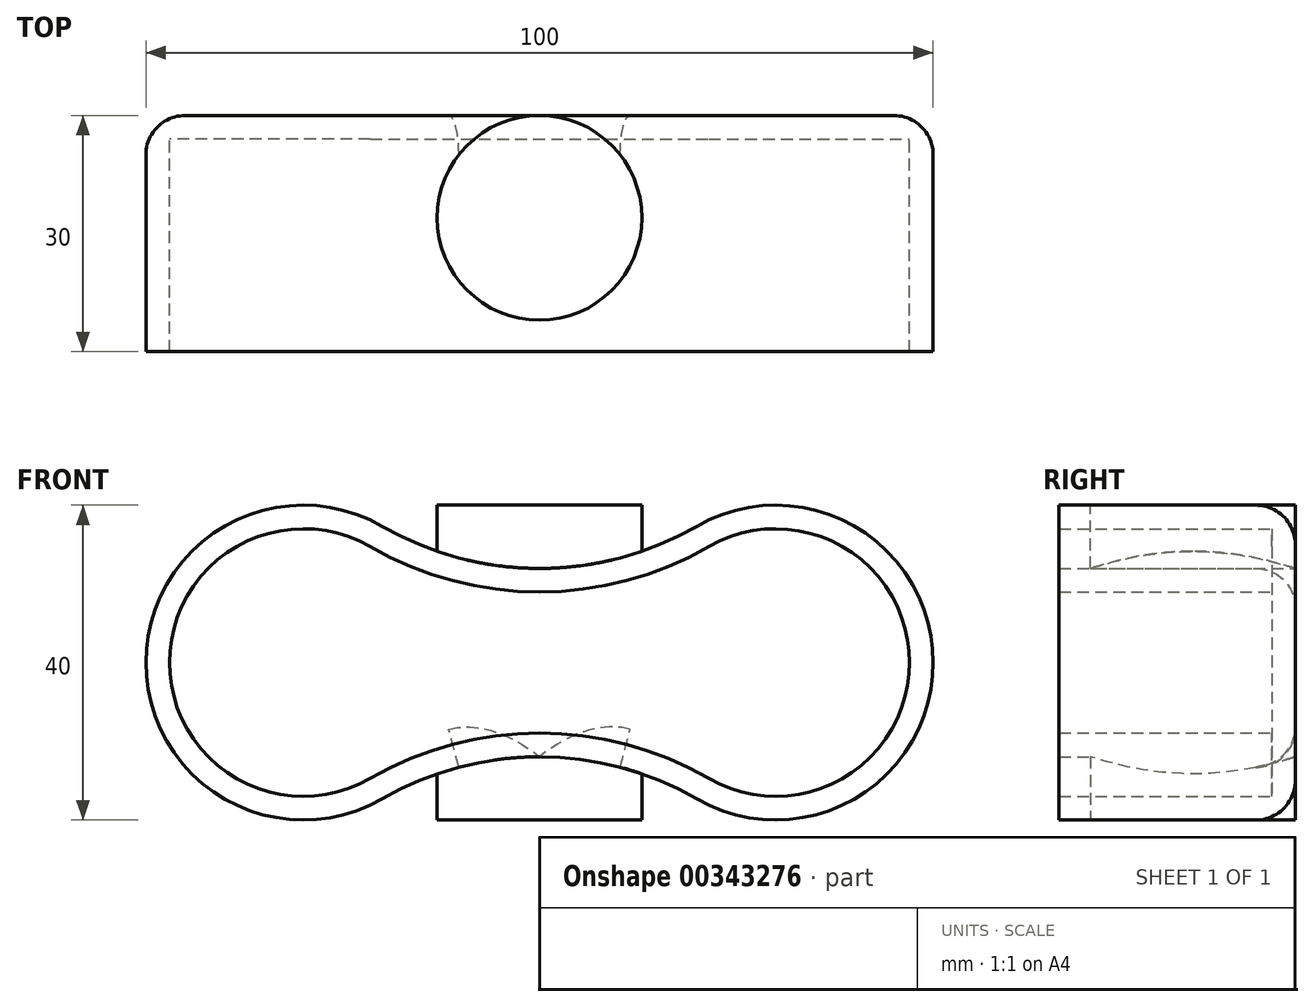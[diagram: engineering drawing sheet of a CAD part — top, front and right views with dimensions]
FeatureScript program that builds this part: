
annotation { "Feature Type Name" : "Feature", "Feature Type Description" : "" }
export const myFeature = defineFeature(function(context is Context, id is Id, definition is map)
    precondition{}
    {
        {
            var Q0;
            Q0=qCreatedBy(makeId("Front.planeOp"),FACE);
            var sketch = newSketch(context, id + "F0", { "sketchPlane" : qUnion([Q0])});
            skArc(sketch, "E0", {"start": v(-20, 17.32) * mm, "mid": v(-50, 0) * mm, "end": v(-20, -17.32) * mm});
            skLineSegment(sketch, "E1", {"start": v(0, 56.7) * mm, "end": v(0, -51.8) * mm, "construction": true});
            skLineSegment(sketch, "E2", {"start": v(-30, 42.91) * mm, "end": v(-30, -37.47) * mm, "construction": true});
            skLineSegment(sketch, "E3", {"start": v(-82.46, 0) * mm, "end": v(56.18, 0) * mm, "construction": true});
            skArc(sketch, "E4", {"start": v(20, -17.32) * mm, "mid": v(0, -11.96) * mm, "end": v(-20, -17.32) * mm});
            skArc(sketch, "E5", {"start": v(20, -17.32) * mm, "mid": v(50, 0) * mm, "end": v(20, 17.32) * mm});
            skArc(sketch, "E6", {"start": v(-20, 17.32) * mm, "mid": v(0, 11.96) * mm, "end": v(20, 17.32) * mm});
            skLineSegment(sketch, "E7", {"start": v(-11.98, 0) * mm, "end": v(72.4, 0) * mm, "construction": true});
            skLineSegment(sketch, "E8", {"start": v(30, 35.28) * mm, "end": v(30, -28.23) * mm, "construction": true});
            skSolve(sketch);
        }
        {
            var Q0;
            Q0 = qSketchRegion(id + "F0", true);
            extrude(context, id + "F1", {"entities" : qUnion([Q0]), "depth" : 30 * mm, "offsetDistance" : 25 * mm});
        }
        {
            var Q0;
            Q0=makeQuery(id+"F1.opExtrude","CAP_FACE",FACE,{"disambiguationData":[OSD([sQuery(id+"F0.wireOp",EDGE,"E0"),sQuery(id+"F0.wireOp",EDGE,"E4"),sQuery(id+"F0.wireOp",EDGE,"E5"),sQuery(id+"F0.wireOp",EDGE,"E6")])],"isStart":false});
            shell(context, id + "F2", {"entities" : qUnion([Q0]), "thickness" : 3 * mm});
        }
        {
            var Q0;
            Q0=qCreatedBy(makeId("Top.planeOp"),FACE);
            cPlane(context, id + "F3", {"entities" : qUnion([Q0]), "cplaneType" : CPlaneType.OFFSET, "offset" : (20) * mm, "oppositeDirection" : true, "width" : 150 * mm, "height" : 150 * mm});
        }
        {
            var Q0;
            Q0=qCreatedBy(id+"F3.planeOp",FACE);
            var sketch = newSketch(context, id + "F4", { "sketchPlane" : qUnion([Q0])});
            skLineSegment(sketch, "E9", {"start": v(-96.09, -13) * mm, "end": v(134.38, -13) * mm, "construction": true});
            skCircle(sketch, "E10", {"center": v(0, -13) * mm, "radius": 13 * mm});
            skSolve(sketch);
        }
        {
            var Q0;
            Q0 = qSketchRegion(id + "F4", true);
            var Q1;
            Q1=makeQuery(id+"F1.opExtrude","SWEPT_FACE",FACE,{"disambiguationData":[OSD([sQuery(id+"F0.wireOp",EDGE,"E4")])]});
            extrude(context, id + "F5", {"entities" : qUnion([Q0]), "operationType" : NewBodyOperationType.ADD, "endBound" : BoundingType.UP_TO_SURFACE, "depth" : 0 * mm, "endBoundEntityFace" : qUnion([Q1]), "offsetDistance" : 25 * mm});
        }
        {
            var Q0;
            Q0=qCreatedBy(makeId("Top.planeOp"),FACE);
            cPlane(context, id + "F6", {"entities" : qUnion([Q0]), "cplaneType" : CPlaneType.OFFSET, "offset" : 20 * mm, "width" : 150 * mm, "height" : 150 * mm});
        }
        {
            var Q0;
            Q0=qCreatedBy(id+"F6.planeOp",FACE);
            var sketch = newSketch(context, id + "F7", { "sketchPlane" : qUnion([Q0])});
            skLineSegment(sketch, "E11", {"start": v(82.93, -13) * mm, "end": v(-96.44, -13) * mm, "construction": true});
            skCircle(sketch, "E12", {"center": v(0, -13) * mm, "radius": 13 * mm});
            skSolve(sketch);
        }
        {
            var Q0;
            Q0 = qSketchRegion(id + "F7", true);
            var Q1;
            Q1=makeQuery(id+"F1.opExtrude","SWEPT_FACE",FACE,{"disambiguationData":[OSD([sQuery(id+"F0.wireOp",EDGE,"E6")])]});
            extrude(context, id + "F8", {"entities" : qUnion([Q0]), "endBound" : BoundingType.UP_TO_SURFACE, "oppositeDirection" : true, "depth" : 25 * mm, "endBoundEntityFace" : qUnion([Q1]), "offsetDistance" : 25 * mm});
        }
        {
            var Q0;
            Q0=makeQuery(id+"F1.opExtrude","CAP_FACE",FACE,{"disambiguationData":[OSD([sQuery(id+"F0.wireOp",EDGE,"E0"),sQuery(id+"F0.wireOp",EDGE,"E4"),sQuery(id+"F0.wireOp",EDGE,"E5"),sQuery(id+"F0.wireOp",EDGE,"E6")])],"isStart":true});
            fillet(context, id + "F9", {"entities" : qUnion([Q0]), "tangentPropagation" : true, "radius" : 5 * mm, "defaultsChanged" : false, "vertexSettings" : [], "allowEdgeOverflow" : false});
        }
    });
